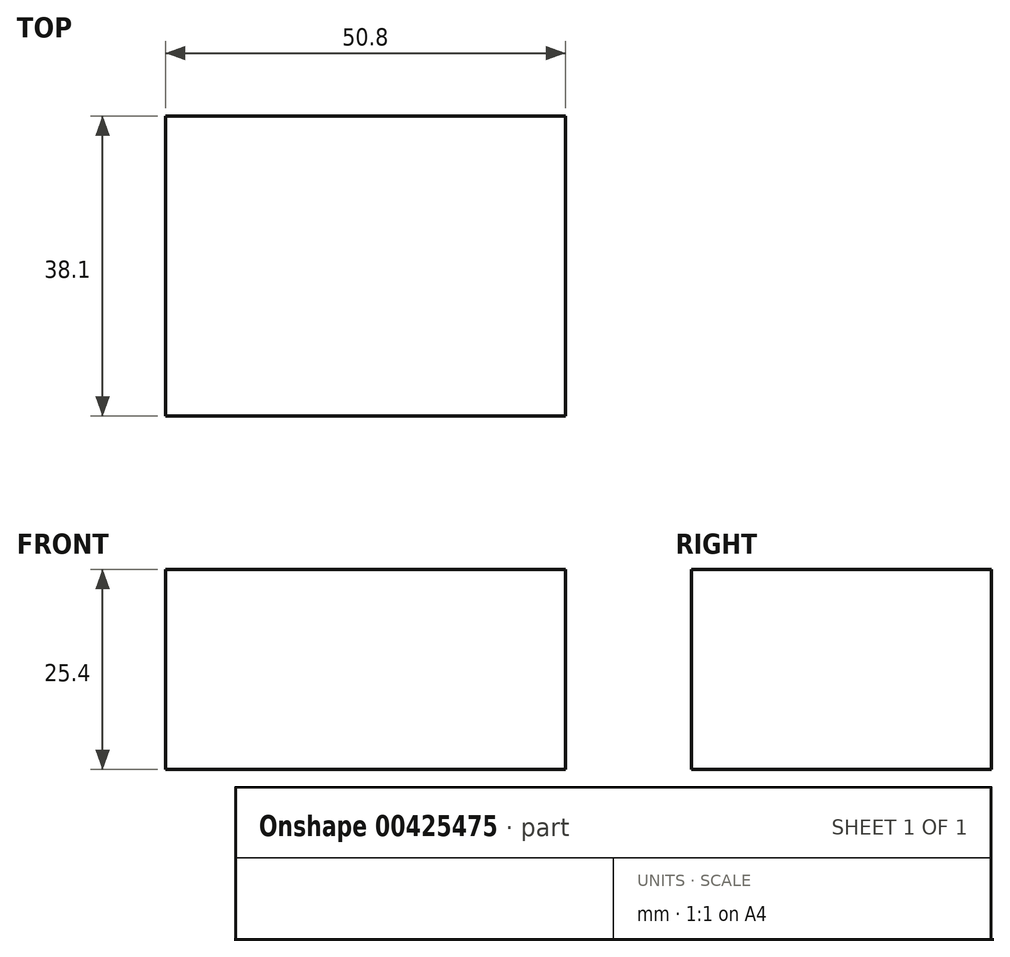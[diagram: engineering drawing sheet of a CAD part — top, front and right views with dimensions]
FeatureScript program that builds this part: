
annotation { "Feature Type Name" : "Feature", "Feature Type Description" : "" }
export const myFeature = defineFeature(function(context is Context, id is Id, definition is map)
    precondition{}
    {
        {
            var Q0;
            Q0=qCreatedBy(makeId("Top.planeOp"),FACE);
            var sketch = newSketch(context, id + "F0", { "sketchPlane" : qUnion([Q0])});
            skLineSegment(sketch, "E0.bottom", {"start": v(25.4, 19.05) * mm, "end": v(-25.4, 19.05) * mm});
            skLineSegment(sketch, "E0.top", {"start": v(25.4, -19.05) * mm, "end": v(-25.4, -19.05) * mm});
            skLineSegment(sketch, "E0.left", {"start": v(25.4, 19.05) * mm, "end": v(25.4, -19.05) * mm});
            skLineSegment(sketch, "E0.right", {"start": v(-25.4, 19.05) * mm, "end": v(-25.4, -19.05) * mm});
            skPoint(sketch, "E0.middle", {"position": v(0, 0) * mm});
            skSolve(sketch);
        }
        {
            var Q0;
            Q0=makeQuery(id+"F0.imprint","IMPRINT",FACE,{"disambiguationData":[TD([[makeQuery(id+"F0.imprint","IMPRINT",EDGE,{"derivedFrom":sQuery(id+"F0.wireOp",EDGE,"E0.bottom")}),1.0]])]});
            extrude(context, id + "F1", {"entities" : qUnion([Q0]), "depth" : 25.4 * mm});
        }
    });
